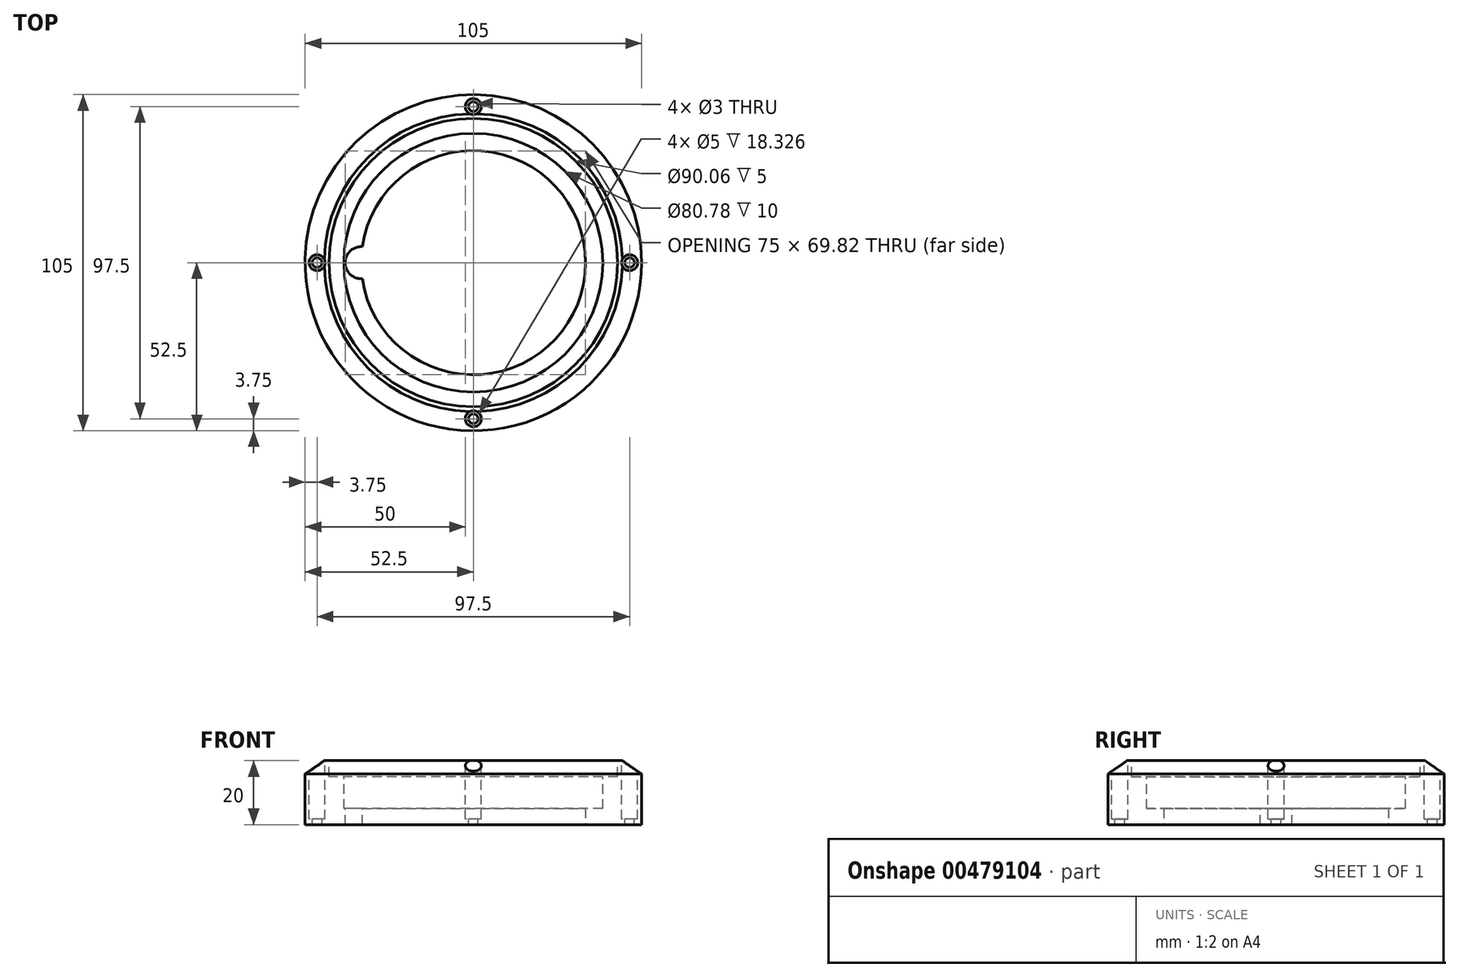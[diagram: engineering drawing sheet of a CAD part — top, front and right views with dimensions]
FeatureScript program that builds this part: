
annotation { "Feature Type Name" : "Feature", "Feature Type Description" : "" }
export const myFeature = defineFeature(function(context is Context, id is Id, definition is map)
    precondition{}
    {
        {
            var Q0;
            Q0=qCreatedBy(makeId("Top.planeOp"),FACE);
            var sketch = newSketch(context, id + "F0", { "sketchPlane" : qUnion([Q0])});
            skCircle(sketch, "E0", {"center": v(0, 0) * mm, "radius": 52.5 * mm});
            skCircle(sketch, "E1", {"center": v(0, 0) * mm, "radius": 35 * mm});
            skSolve(sketch);
        }
        {
            var Q0;
            Q0 = qSketchRegion(id + "F0", true);
            var Q1;
            Q1=makeQuery(id+"F0.imprint","IMPRINT",FACE,{"disambiguationData":[TD([[makeQuery(id+"F0.imprint","IMPRINT",EDGE,{"derivedFrom":sQuery(id+"F0.wireOp",EDGE,"E1")}),1.0]])]});
            extrude(context, id + "F1", {"entities" : qUnion([Q0, Q1]), "depth" : 20 * mm});
        }
        {
            var Q0;
            Q0=makeQuery(id+"F0.imprint","IMPRINT",FACE,{"disambiguationData":[TD([[makeQuery(id+"F0.imprint","IMPRINT",EDGE,{"derivedFrom":sQuery(id+"F0.wireOp",EDGE,"E1")}),1.0]])]});
            extrude(context, id + "F2", {"entities" : qUnion([Q0]), "operationType" : NewBodyOperationType.REMOVE, "depth" : 20 * mm});
        }
        {
            var Q0;
            Q0=makeQuery(id+"F1.opExtrude","CAP_FACE",FACE,{"disambiguationData":[OSD([sQuery(id+"F0.wireOp",EDGE,"E0")])],"isStart":false});
            var sketch = newSketch(context, id + "F3", { "sketchPlane" : qUnion([Q0])});
            skCircle(sketch, "E2", {"center": v(0, 0) * mm, "radius": 45.03 * mm});
            skSolve(sketch);
        }
        {
            var Q0;
            Q0=makeQuery(id+"F3.imprint","IMPRINT",FACE,{"disambiguationData":[TD([[makeQuery(id+"F3.imprint","IMPRINT",EDGE,{"derivedFrom":sQuery(id+"F3.wireOp",EDGE,"E2")}),1.0]])]});
            extrude(context, id + "F4", {"entities" : qUnion([Q0]), "operationType" : NewBodyOperationType.REMOVE, "oppositeDirection" : true, "depth" : 5 * mm});
        }
        {
            var Q0;
            Q0=makeQuery(id+"F1.opExtrude","CAP_EDGE",EDGE,{"disambiguationData":[OSD([sQuery(id+"F0.wireOp",EDGE,"E0")])],"isStart":false});
            chamfer(context, id + "F5", {"entities" : qUnion([Q0]), "chamferType" : ChamferType.OFFSET_ANGLE, "width" : 6 * mm, "oppositeDirection" : false, "angle" : 35 * degree, "tangentPropagation" : true});
        }
        {
            var Q0;
            Q0=makeQuery(id+"F1.opExtrude","CAP_FACE",FACE,{"disambiguationData":[OSD([sQuery(id+"F0.wireOp",EDGE,"E0")])],"isStart":false});
            var sketch = newSketch(context, id + "F6", { "sketchPlane" : qUnion([Q0])});
            skCircle(sketch, "E3.cCircle", {"center": v(0, 0) * mm, "radius": 48.75 * mm, "construction": true});
            skLineSegment(sketch, "E3.0", {"start": v(0, 48.75) * mm, "end": v(48.75, 0) * mm});
            skLineSegment(sketch, "E3.1", {"start": v(48.75, 0) * mm, "end": v(0, -48.75) * mm});
            skLineSegment(sketch, "E3.2", {"start": v(0, -48.75) * mm, "end": v(-48.75, 0) * mm});
            skLineSegment(sketch, "E3.3", {"start": v(-48.75, 0) * mm, "end": v(0, 48.75) * mm});
            skCircle(sketch, "E4", {"center": v(-48.75, 0) * mm, "radius": 1.75 * mm});
            skCircle(sketch, "E5", {"center": v(0, 48.75) * mm, "radius": 1.75 * mm});
            skCircle(sketch, "E6", {"center": v(48.75, 0) * mm, "radius": 1.75 * mm});
            skCircle(sketch, "E7", {"center": v(0, -48.75) * mm, "radius": 1.75 * mm});
            skSolve(sketch);
        }
        {
            var Q0;
            Q0=sQuery(id+"F6.wireOp",VERTEX,"E4.center");
            var Q1;
            Q1=sQuery(id+"F6.wireOp",VERTEX,"E7.center");
            var Q2;
            Q2=sQuery(id+"F6.wireOp",VERTEX,"E6.center");
            var Q3;
            Q3=sQuery(id+"F6.wireOp",VERTEX,"E5.center");
            var Q4;
            Q4=makeQuery(id+"F1.opExtrude","SWEPT_BODY",BODY,{"disambiguationData":[OSD([sQuery(id+"F0.wireOp",EDGE,"E0")])]});
            hole(context, id + "F7", {"style" : HoleStyle.C_BORE, "endStyle" : HoleEndStyle.THROUGH, "holeDiameter" : 3 * mm, "cBoreDiameter" : 5 * mm, "cBoreDepth" : 15 * mm, "isTappedThrough" : true, "tappedDepth" : 12 * mm, "tapClearance" : 3, "locations" : qUnion([Q0, Q1, Q2, Q3]), "scope" : qUnion([Q4])});
        }
        {
            var Q0;
            Q0=makeQuery(id+"F4.boolean.opBoolean","COPY",FACE,{"derivedFrom":makeQuery(id+"F4.opExtrude","CAP_FACE",FACE,{"disambiguationData":[OSD([sQuery(id+"F0.wireOp",EDGE,"E1"),sQuery(id+"F3.wireOp",EDGE,"E2")])],"isStart":false})});
            var sketch = newSketch(context, id + "F8", { "sketchPlane" : qUnion([Q0])});
            skCircle(sketch, "E8", {"center": v(0, 0) * mm, "radius": 40.4 * mm});
            skCircle(sketch, "E9", {"center": v(-35, 0) * mm, "radius": 5 * mm});
            skSolve(sketch);
        }
        {
            var Q0;
            Q0=makeQuery(id+"F8.imprint","IMPRINT",FACE,{"disambiguationData":[TD([[makeQuery(id+"F8.imprint","IMPRINT",EDGE,{"derivedFrom":sQuery(id+"F8.wireOp",EDGE,"E8")}),1.0]])]});
            extrude(context, id + "F9", {"entities" : qUnion([Q0]), "operationType" : NewBodyOperationType.REMOVE, "oppositeDirection" : true, "depth" : 10 * mm});
        }
        {
            var Q0;
            {var subQ0=sQuery(id+"F0.wireOp",EDGE,"E1");Q0=makeQuery(id+"F9.boolean.opBoolean","SPLIT",FACE,{"disambiguationData":[TD([makeQuery(id+"F2.boolean.opBoolean","COPY",FACE,{"derivedFrom":makeQuery(id+"F2.opExtrude","SWEPT_FACE",FACE,{"disambiguationData":[OSD([subQ0])]})})])],"derivedFrom":makeQuery(id+"F4.boolean.opBoolean","COPY",FACE,{"derivedFrom":makeQuery(id+"F4.opExtrude","CAP_FACE",FACE,{"disambiguationData":[OSD([subQ0,sQuery(id+"F3.wireOp",EDGE,"E2")])],"isStart":false})})});}
            extrude(context, id + "F10", {"entities" : qUnion([Q0]), "operationType" : NewBodyOperationType.REMOVE, "oppositeDirection" : true, "depth" : 50 * mm});
        }
    });
